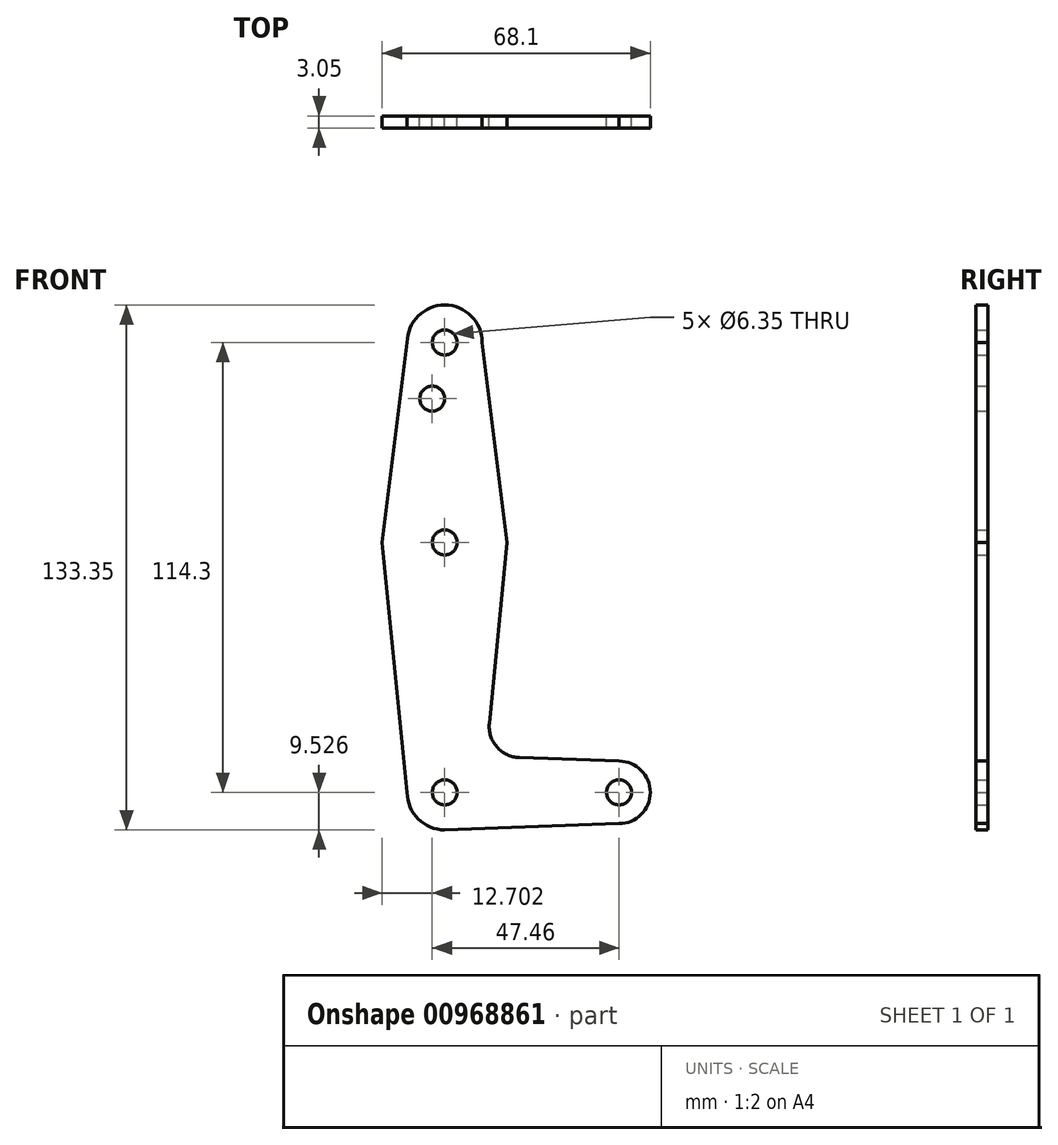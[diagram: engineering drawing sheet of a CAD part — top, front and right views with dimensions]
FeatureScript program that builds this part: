
annotation { "Feature Type Name" : "Feature", "Feature Type Description" : "" }
export const myFeature = defineFeature(function(context is Context, id is Id, definition is map)
    precondition{}
    {
        {
            var Q0;
            Q0=qCreatedBy(makeId("Front.planeOp"),FACE);
            var sketch = newSketch(context, id + "F0", { "sketchPlane" : qUnion([Q0])});
            skLineSegment(sketch, "E0", {"start": v(20.09, 63.85) * mm, "end": v(20.09, -50.45) * mm, "construction": true});
            skCircle(sketch, "E1", {"center": v(20.09, 63.85) * mm, "radius": 9.53 * mm});
            skCircle(sketch, "E2", {"center": v(20.09, 13.05) * mm, "radius": 15.88 * mm});
            skCircle(sketch, "E3", {"center": v(20.09, -50.45) * mm, "radius": 9.53 * mm});
            skCircle(sketch, "E4", {"center": v(64.37, -50.45) * mm, "radius": 7.94 * mm});
            skPoint(sketch, "E5", {"position": v(21.83, 73.21) * mm});
            skLineSegment(sketch, "E6", {"start": v(20.09, 63.85) * mm, "end": v(10.56, 63.85) * mm, "construction": true});
            skLineSegment(sketch, "E7", {"start": v(20.09, 13.05) * mm, "end": v(4.21, 13.05) * mm, "construction": true});
            skLineSegment(sketch, "E8", {"start": v(20.09, -50.45) * mm, "end": v(10.56, -50.45) * mm, "construction": true});
            skLineSegment(sketch, "E9", {"start": v(10.56, -50.45) * mm, "end": v(20.09, -50.45) * mm, "construction": true});
            skLineSegment(sketch, "E10", {"start": v(10.56, 63.85) * mm, "end": v(4.21, 13.05) * mm});
            skLineSegment(sketch, "E11", {"start": v(4.21, 13.05) * mm, "end": v(10.56, -50.45) * mm});
            skLineSegment(sketch, "E12", {"start": v(20.09, -50.45) * mm, "end": v(64.37, -50.45) * mm, "construction": true});
            skLineSegment(sketch, "E13", {"start": v(10.56, 63.85) * mm, "end": v(29.61, 63.85) * mm, "construction": true});
            skLineSegment(sketch, "E14", {"start": v(20.09, 13.05) * mm, "end": v(35.96, 13.05) * mm, "construction": true});
            skLineSegment(sketch, "E15", {"start": v(64.37, -50.45) * mm, "end": v(64.37, -42.52) * mm, "construction": true});
            skLineSegment(sketch, "E16", {"start": v(64.37, -42.52) * mm, "end": v(64.37, -58.4) * mm, "construction": true});
            skLineSegment(sketch, "E17", {"start": v(29.61, 63.85) * mm, "end": v(35.96, 13.05) * mm});
            skLineSegment(sketch, "E18", {"start": v(35.96, 13.05) * mm, "end": v(31.4, -32.88) * mm});
            skLineSegment(sketch, "E19", {"start": v(39.03, -41.6) * mm, "end": v(64.37, -42.52) * mm});
            skLineSegment(sketch, "E20", {"start": v(20.09, -59.98) * mm, "end": v(64.37, -58.4) * mm});
            skCircle(sketch, "E21", {"center": v(20.09, 63.85) * mm, "radius": 3.18 * mm});
            skCircle(sketch, "E22", {"center": v(20.09, 13.05) * mm, "radius": 3.18 * mm});
            skCircle(sketch, "E23", {"center": v(20.09, -50.45) * mm, "radius": 3.18 * mm});
            skCircle(sketch, "E24", {"center": v(64.37, -50.45) * mm, "radius": 3.18 * mm});
            skCircle(sketch, "E25", {"center": v(16.91, 49.57) * mm, "radius": 3.18 * mm});
            skPoint(sketch, "E26.newPointA", {"position": v(29.61, -50.93) * mm});
            skArc(sketch, "E26.filletArc", {"start": v(31.4, -32.88) * mm, "mid": v(33.33, -38.9) * mm, "end": v(39.03, -41.6) * mm});
            skSolve(sketch);
        }
        {
            var Q0;
            Q0=makeQuery(id+"F0.imprint","IMPRINT",FACE,{"disambiguationData":[TD([[makeQuery(id+"F0.imprint","IMPRINT",EDGE,{"derivedFrom":sQuery(id+"F0.wireOp",EDGE,"E25")}),-1.0]])]});
            var Q1;
            Q1=makeQuery(id+"F0.imprint","IMPRINT",FACE,{"disambiguationData":[TD([[makeQuery(id+"F0.imprint","IMPRINT",EDGE,{"derivedFrom":sQuery(id+"F0.wireOp",EDGE,"E21")}),-1.0]])]});
            var Q2;
            Q2=makeQuery(id+"F0.imprint","IMPRINT",FACE,{"disambiguationData":[TD([[makeQuery(id+"F0.imprint","IMPRINT",EDGE,{"derivedFrom":sQuery(id+"F0.wireOp",EDGE,"E22")}),-1.0]])]});
            var Q3;
            {var subQ5=sQuery(id+"F0.wireOp",EDGE,"E19");Q3=makeQuery(id+"F0.imprint","IMPRINT",FACE,{"disambiguationData":[TD([[makeQuery(id+"F0.imprint","IMPRINT",EDGE,{"derivedFrom":subQ5}),-1.0]])]});}
            var Q4;
            Q4=makeQuery(id+"F0.imprint","IMPRINT",FACE,{"disambiguationData":[TD([[makeQuery(id+"F0.imprint","IMPRINT",EDGE,{"derivedFrom":sQuery(id+"F0.wireOp",EDGE,"E24")}),-1.0]])]});
            var Q5;
            Q5=makeQuery(id+"F0.imprint","IMPRINT",FACE,{"disambiguationData":[TD([[makeQuery(id+"F0.imprint","IMPRINT",EDGE,{"derivedFrom":sQuery(id+"F0.wireOp",EDGE,"E23")}),-1.0]])]});
            extrude(context, id + "F1", {"entities" : qUnion([Q0, Q1, Q2, Q3, Q4, Q5]), "depth" : 3.05 * mm, "offsetDistance" : 25.4 * mm});
        }
    });
